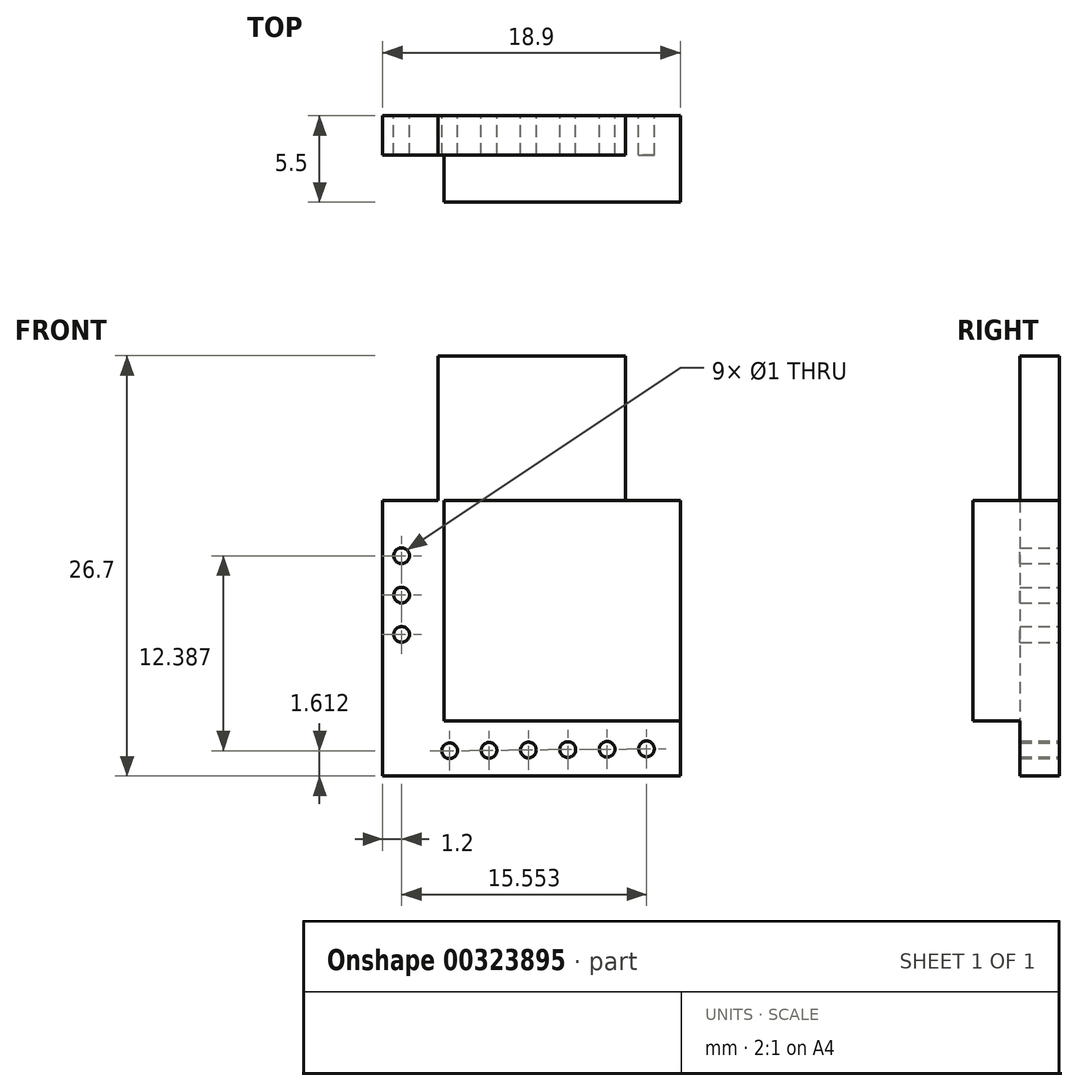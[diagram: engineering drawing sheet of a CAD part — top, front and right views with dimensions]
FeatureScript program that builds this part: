
annotation { "Feature Type Name" : "Feature", "Feature Type Description" : "" }
export const myFeature = defineFeature(function(context is Context, id is Id, definition is map)
    precondition{}
    {
        {
            var Q0;
            Q0=qCreatedBy(makeId("Front.planeOp"),FACE);
            var sketch = newSketch(context, id + "F0", { "sketchPlane" : qUnion([Q0])});
            skLineSegment(sketch, "E0.bottom", {"start": v(-1.2, 19) * mm, "end": v(17.7, 19) * mm});
            skLineSegment(sketch, "E0.top", {"start": v(-1.2, 1.5) * mm, "end": v(17.7, 1.5) * mm});
            skLineSegment(sketch, "E0.right", {"start": v(17.7, 19) * mm, "end": v(17.7, 1.5) * mm});
            skLineSegment(sketch, "E1.bottom", {"start": v(14.2, 28.2) * mm, "end": v(2.3, 28.2) * mm});
            skLineSegment(sketch, "E1.left", {"start": v(14.2, 28.2) * mm, "end": v(14.2, 19) * mm});
            skLineSegment(sketch, "E1.right", {"start": v(2.3, 28.2) * mm, "end": v(2.3, 19) * mm});
            skLineSegment(sketch, "E2.bottom", {"start": v(-1.2, 19) * mm, "end": v(14.1, 19) * mm});
            skLineSegment(sketch, "E2.left", {"start": v(-1.2, 19) * mm, "end": v(-1.2, 1.5) * mm});
            skLineSegment(sketch, "E3.bottom", {"start": v(-1.2, 19) * mm, "end": v(14.5, 19) * mm});
            skLineSegment(sketch, "E4.bottom", {"start": v(-1.2, 19) * mm, "end": v(14.86, 19) * mm});
            skLineSegment(sketch, "E5.bottom", {"start": v(17.7, 19) * mm, "end": v(2.7, 19) * mm});
            skLineSegment(sketch, "E5.top", {"start": v(17.7, 5) * mm, "end": v(2.7, 5) * mm});
            skLineSegment(sketch, "E5.left", {"start": v(17.7, 19) * mm, "end": v(17.7, 5) * mm});
            skLineSegment(sketch, "E5.right", {"start": v(2.7, 19) * mm, "end": v(2.7, 5) * mm});
            skCircle(sketch, "E6", {"center": v(0, 15.5) * mm, "radius": 0.5 * mm});
            skCircle(sketch, "E7.1.0.0", {"center": v(0, 13) * mm, "radius": 0.5 * mm});
            skCircle(sketch, "E7.2.0.0", {"center": v(0, 10.5) * mm, "radius": 0.5 * mm});
            skLineSegment(sketch, "E7.direction1", {"start": v(0, 15.5) * mm, "end": v(0, 13) * mm, "construction": true});
            skCircle(sketch, "E8", {"center": v(15.55, 3.24) * mm, "radius": 0.5 * mm});
            skCircle(sketch, "E9.1.0.0", {"center": v(13.05, 3.22) * mm, "radius": 0.5 * mm});
            skCircle(sketch, "E9.2.0.0", {"center": v(10.55, 3.2) * mm, "radius": 0.5 * mm});
            skCircle(sketch, "E9.3.0.0", {"center": v(8.05, 3.17) * mm, "radius": 0.5 * mm});
            skCircle(sketch, "E9.4.0.0", {"center": v(5.55, 3.15) * mm, "radius": 0.5 * mm});
            skCircle(sketch, "E9.5.0.0", {"center": v(3.05, 3.12) * mm, "radius": 0.5 * mm});
            skLineSegment(sketch, "E9.direction1", {"start": v(15.55, 3.24) * mm, "end": v(13.05, 3.22) * mm, "construction": true});
            skSolve(sketch);
        }
        {
            var Q0;
            Q0=makeQuery(id+"F0.imprint","IMPRINT",FACE,{"disambiguationData":[TD([[makeQuery(id+"F0.imprint","IMPRINT",EDGE,{"derivedFrom":sQuery(id+"F0.wireOp",EDGE,"E5.top")}),-1.0]])]});
            extrude(context, id + "F1", {"entities" : qUnion([Q0]), "depth" : 5.5 * mm});
        }
        {
            var Q0;
            Q0 = qSketchRegion(id + "F0", true);
            extrude(context, id + "F2", {"entities" : qUnion([Q0]), "operationType" : NewBodyOperationType.ADD, "depth" : 2.5 * mm});
        }
    });
